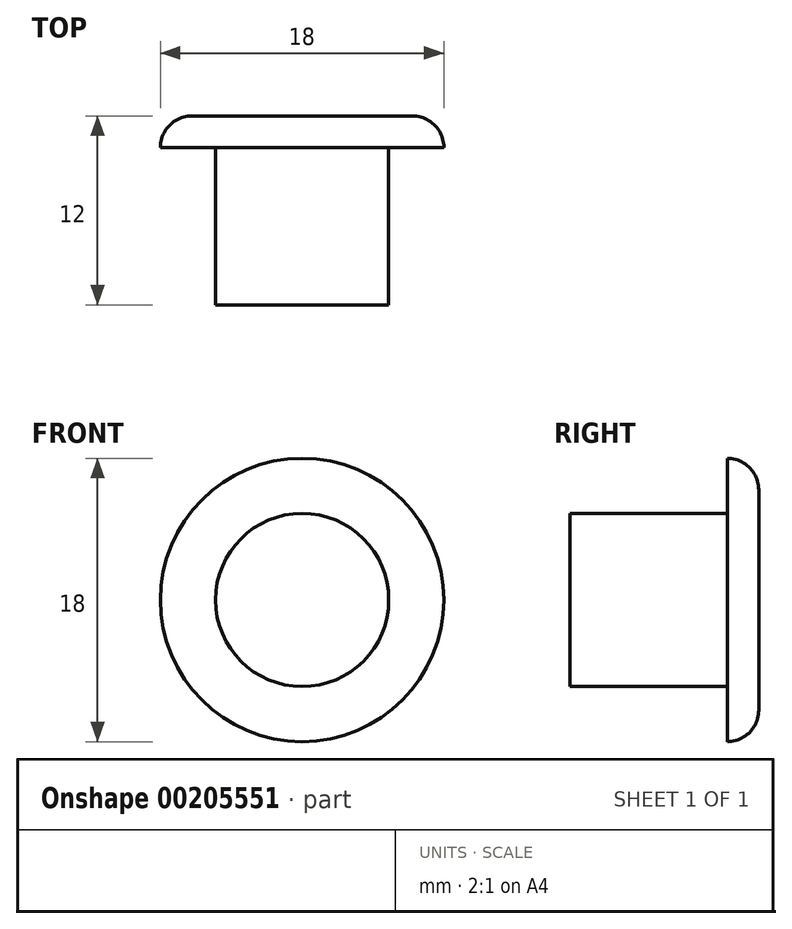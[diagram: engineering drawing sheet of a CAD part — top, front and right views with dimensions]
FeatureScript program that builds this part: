
annotation { "Feature Type Name" : "Feature", "Feature Type Description" : "" }
export const myFeature = defineFeature(function(context is Context, id is Id, definition is map)
    precondition{}
    {
        {
            var Q0;
            Q0=qCreatedBy(makeId("Front.planeOp"),FACE);
            var sketch = newSketch(context, id + "F0", { "sketchPlane" : qUnion([Q0])});
            skCircle(sketch, "E0", {"center": v(0, 0) * mm, "radius": 9 * mm});
            skSolve(sketch);
        }
        {
            var Q0;
            Q0=qSketchRegion(id+"F0",true);
            extrude(context, id + "F1", {"entities" : qUnion([Q0]), "depth" : 12 * mm});
        }
        {
            var Q0;
            Q0=makeQuery(id+"F1.opExtrude","CAP_FACE",FACE,{"disambiguationData":[OSD([sQuery(id+"F0.wireOp",EDGE,"E0")])],"isStart":false});
            var sketch = newSketch(context, id + "F2", { "sketchPlane" : qUnion([Q0])});
            skCircle(sketch, "E1", {"center": v(0, 0) * mm, "radius": 5.5 * mm});
            skSolve(sketch);
        }
        {
            var Q0;
            Q0=makeQuery(id+"F1.opExtrude","CAP_FACE",FACE,{"disambiguationData":[OSD([sQuery(id+"F0.wireOp",EDGE,"E0")])],"isStart":true});
            fillet(context, id + "F3", {"entities" : qUnion([Q0]), "radius" : 2 * mm, "tangentPropagation" : true, "allowEdgeOverflow" : false});
        }
        {
            var Q0;
            Q0=makeQuery(id+"F2.imprint","IMPRINT",FACE,{"disambiguationData":[TD([[makeQuery(id+"F2.imprint","IMPRINT",EDGE,{"derivedFrom":sQuery(id+"F2.wireOp",EDGE,"E1")}),-1.0]])]});
            extrude(context, id + "F4", {"entities" : qUnion([Q0]), "operationType" : NewBodyOperationType.REMOVE, "oppositeDirection" : true, "depth" : 10 * mm});
        }
    });
